# Revit family: ledpanels-p6_re295-34w-940-u19_542003113500
name_source: partatom
category: Leuchten
revit_build: Autodesk Revit 2016 (Build: 20190508_0715(x64)
units: mm (PartAtom-declared; Revit-internal decimal feet)

## family parameters
Basisbauteil = Fläche
Beim Laden mit Abzugskörper schneiden = Nein
Bemaßung runder Anschluss = Durchmesser verwenden
Gemeinsam genutzt = Nein
Lichtquelle = Nein
Raumberechnungspunkt = Nein
Teiletyp = Normal

## types (1)
- LEDPanelS-P6 Re295-34W-940-U19 (1 x LED, 4080 lm, 4000)
    Approval mark = CE, ENEC
    Beschreibung = High quality LED Slim Panel, suitable for offices (UGR19). Standard IP54 (front side). Recessed, suspended and surface mounting possible.
    CIE Flux Codes = 61 88 97 100 100
    Color Rendering = 90
    Color Temperature = 4000
    Control Gear = Electronic ballast
    Frequency = 60 Hz
    Height = 25 mm  [stored 0.082021 ft]
    Hersteller = OPPLE
    Lamp Light Flux = 4080 lm
    Lamp count = 1
    Lampe = 1 x LED
    Length = 1195 mm
    Luminous efficacy = 120 lm/W
    ModVariant = Nein
    Modell = 542003113500
    Mounting Place = Ceiling, Pole
    Mounting Type = Recessed, Pendant
    Number of Poles = 1
    OnlyDefault = Ja
    Power Factor = 1
    Product Name = LEDPanelS-P6 Re295-34W-940-U19
    Product group = Ceiling mounted luminaire
    ProductGroupID = 3
    Protection Class = Protection class II
    Protection Degree = IP 54
    RLX_Detail_Level = 1
    RlxData = <blob elided: 90597 chars, md5=06ae2a6b>
    Scheinlast = 34 VA
    Socket = socket
    Standby Power = 0 W
    System Light Flux = 4080 lm
    System Power = 34 W
    Typenbild = web_slimp_p6_re295.jpg
    Typenkommentare = Product without accessories
    URL = http://relux.com
    VarID = ---
    Voltage = 230 V
    Voltage Range = 220-240 V
    Vorgabe-Ansicht = 1800 mm
    Weight = 0.00 kg
    Width = 295 mm

note: [stored X ft] marks values corroborated as IEEE doubles in the binary element streams (Revit-internal decimal feet)

## geometry (parser evidence)
native form markers: Blend x4, Sweep x14
no freeform markers — native parametric forms only
